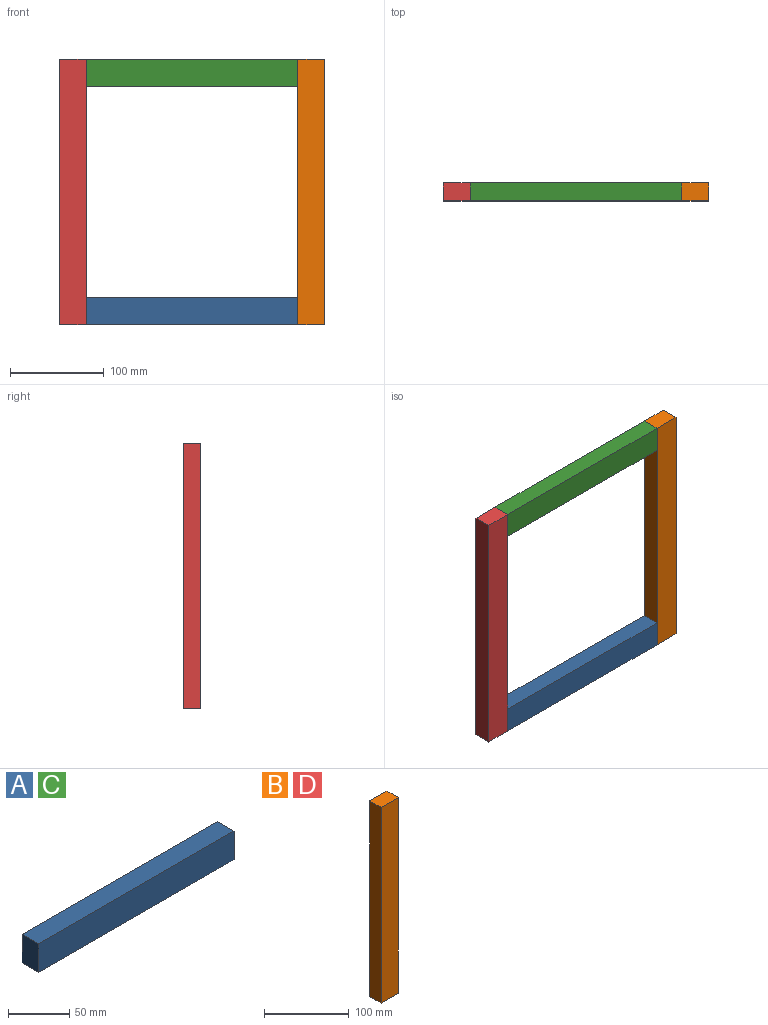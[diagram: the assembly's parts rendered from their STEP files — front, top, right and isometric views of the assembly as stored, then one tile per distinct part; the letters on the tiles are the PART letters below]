
ASSEMBLY  parts=4 mates=9
PART A: 6 faces, bbox 225.4x19.1x28.6 mm
  f0: plane 28.58x19.05mm, normal (-1,0,0), area 544.4mm2, adj f1,f3,f4,f5
  f1: plane 225.43x19.05mm, normal (0,0,-1), area 4294.3mm2, adj f0,f2,f4,f5
  f2: plane 28.58x19.05mm, normal (1,0,0), area 544.4mm2, adj f1,f3,f4,f5
  f3: plane 225.43x19.05mm, normal (0,0,1), area 4294.3mm2, adj f0,f2,f4,f5
  f4: plane 225.43x28.58mm, normal (0,-1,0), area 6441.5mm2, adj f0,f1,f2,f3
  f5: plane 225.43x28.58mm, normal (0,1,0), area 6441.5mm2, adj f0,f1,f2,f3
PART B: 6 faces, bbox 28.6x19.1x282.6 mm
  f0: plane 28.58x19.05mm, normal (0,0,-1), area 544.4mm2, adj f1,f3,f4,f5
  f1: plane 282.58x19.05mm, normal (1,0,0), area 5383.1mm2, adj f0,f2,f4,f5
  f2: plane 28.58x19.05mm, normal (0,0,1), area 544.4mm2, adj f1,f3,f4,f5
  f3: plane 282.58x19.05mm, normal (-1,0,0), area 5383.1mm2, adj f0,f2,f4,f5
  f4: plane 282.58x28.58mm, normal (0,-1,0), area 8074.6mm2, adj f0,f1,f2,f3
  f5: plane 282.58x28.58mm, normal (0,1,0), area 8074.6mm2, adj f0,f1,f2,f3
PART C: same geometry as A
PART D: same geometry as B
PLACE A t=(72.11,14.7,-262.06)mm
PLACE B t=(326.11,14.7,-8.06)mm
PLACE C t=(72.11,14.7,-8.06)mm
PLACE D t=(72.11,14.7,-8.06)mm
MATE planar D.f4 <-> B.f4  axis (0,-1,0) through (57.83,-4.35,-8.06)mm
MATE planar A.f1 <-> D.f0  axis (0,0,-1) through (184.83,5.17,-290.63)mm
MATE planar D.f4 <-> C.f4  axis (0,-1,0) through (57.83,-4.35,-149.34)mm
MATE planar C.f3 <-> B.f2  axis (0,0,1) through (184.83,5.17,-8.06)mm
MATE planar C.f0 <-> D.f1  axis (-1,0,0) through (72.11,5.17,-22.34)mm
MATE planar A.f4 <-> D.f4  axis (0,-1,0) through (184.83,-4.35,-276.34)mm
MATE planar C.f3 <-> D.f2  axis (0,0,1) through (184.83,5.17,-8.06)mm
MATE planar A.f0 <-> D.f1  axis (-1,0,0) through (72.11,5.17,-276.34)mm
MATE planar C.f2 <-> B.f3  axis (1,0,0) through (297.54,5.17,-22.34)mm
